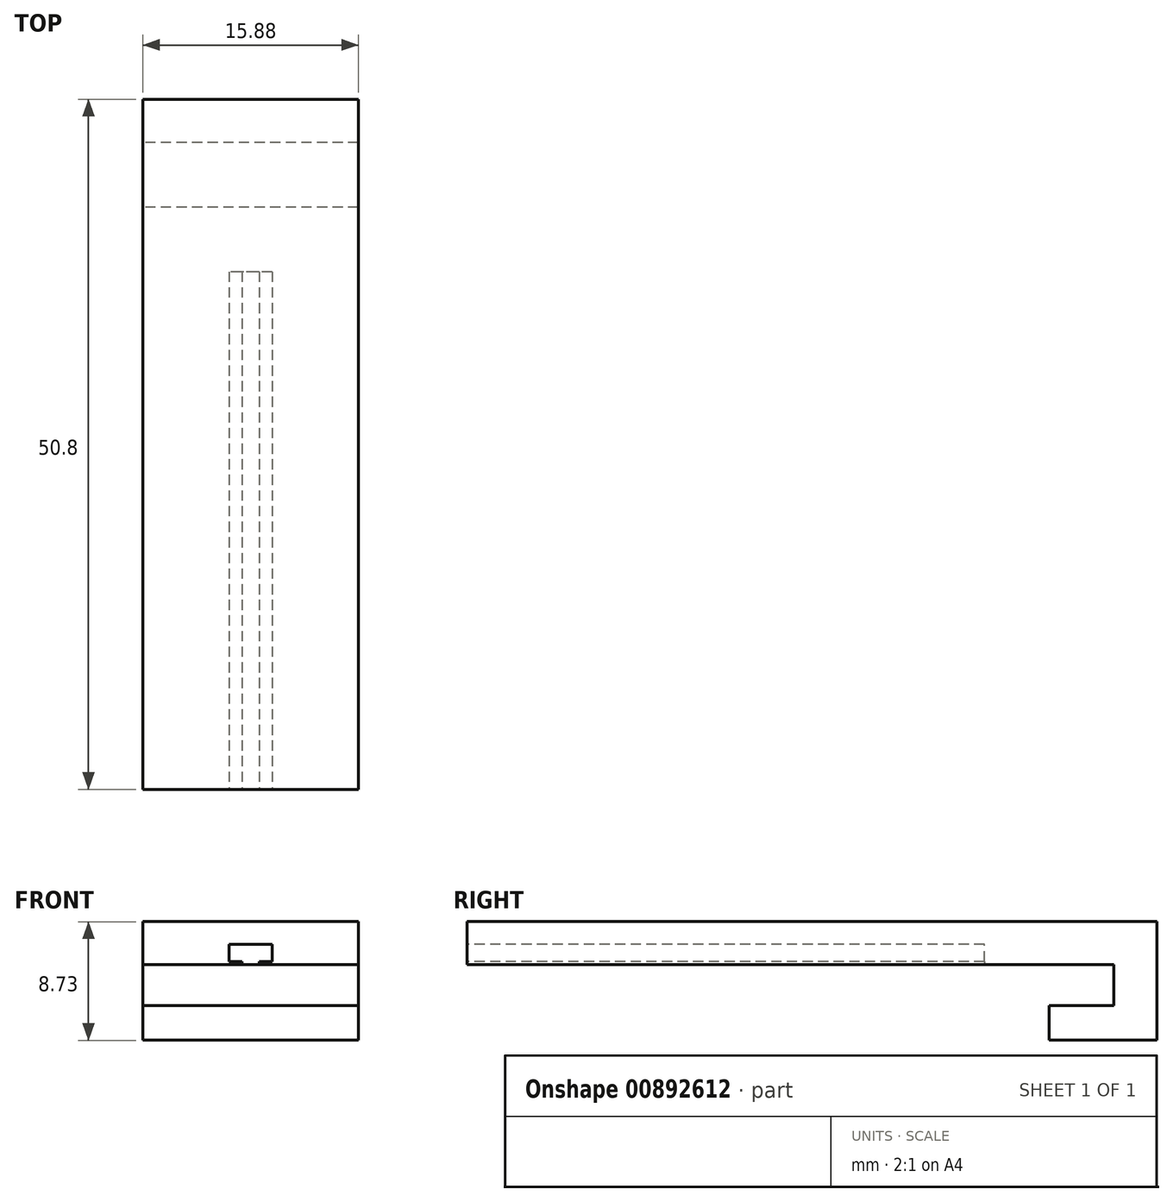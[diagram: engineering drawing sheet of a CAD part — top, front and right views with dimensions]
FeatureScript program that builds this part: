
annotation { "Feature Type Name" : "Feature", "Feature Type Description" : "" }
export const myFeature = defineFeature(function(context is Context, id is Id, definition is map)
    precondition{}
    {
        {
            var Q0;
            Q0=qCreatedBy(makeId("Top.planeOp"),FACE);
            var sketch = newSketch(context, id + "F0", { "sketchPlane" : qUnion([Q0])});
            skLineSegment(sketch, "E0.bottom", {"start": v(7.94, -25.4) * mm, "end": v(-7.94, -25.4) * mm});
            skLineSegment(sketch, "E0.top", {"start": v(7.94, 25.4) * mm, "end": v(-7.94, 25.4) * mm});
            skLineSegment(sketch, "E0.left", {"start": v(7.94, -25.4) * mm, "end": v(7.94, 25.4) * mm});
            skLineSegment(sketch, "E0.right", {"start": v(-7.94, -25.4) * mm, "end": v(-7.94, 25.4) * mm});
            skPoint(sketch, "E0.middle", {"position": v(0, 0) * mm});
            skSolve(sketch);
        }
        {
            var Q0;
            Q0=makeQuery(id+"F0.imprint","IMPRINT",FACE,{"disambiguationData":[TD([[makeQuery(id+"F0.imprint","IMPRINT",EDGE,{"derivedFrom":sQuery(id+"F0.wireOp",EDGE,"E0.bottom")}),-1.0]])]});
            extrude(context, id + "F1", {"entities" : qUnion([Q0]), "depth" : 3.17 * mm, "offsetDistance" : 25.4 * mm});
        }
        {
            var Q0;
            Q0=makeQuery(id+"F1.opExtrude","CAP_FACE",FACE,{"disambiguationData":[OSD([sQuery(id+"F0.wireOp",EDGE,"E0.bottom"),sQuery(id+"F0.wireOp",EDGE,"E0.top"),sQuery(id+"F0.wireOp",EDGE,"E0.left"),sQuery(id+"F0.wireOp",EDGE,"E0.right")])],"isStart":true});
            var sketch = newSketch(context, id + "F2", { "sketchPlane" : qUnion([Q0])});
            skLineSegment(sketch, "E1.bottom", {"start": v(7.94, -25.4) * mm, "end": v(-7.94, -25.4) * mm});
            skLineSegment(sketch, "E1.top", {"start": v(7.94, -22.23) * mm, "end": v(-7.94, -22.23) * mm});
            skLineSegment(sketch, "E1.left", {"start": v(7.94, -25.4) * mm, "end": v(7.94, -22.23) * mm});
            skLineSegment(sketch, "E1.right", {"start": v(-7.94, -25.4) * mm, "end": v(-7.94, -22.23) * mm});
            skSolve(sketch);
        }
        {
            var Q0;
            Q0=makeQuery(id+"F2.imprint","IMPRINT",FACE,{"disambiguationData":[TD([[makeQuery(id+"F2.imprint","IMPRINT",EDGE,{"derivedFrom":sQuery(id+"F2.wireOp",EDGE,"E1.bottom")}),-1.0]])]});
            extrude(context, id + "F3", {"entities" : qUnion([Q0]), "operationType" : NewBodyOperationType.ADD, "depth" : 5.56 * mm, "offsetDistance" : 25.4 * mm});
        }
        {
            var Q0;
            Q0=makeQuery(id+"F3.opExtrude","SWEPT_FACE",FACE,{"disambiguationData":[OSD([sQuery(id+"F2.wireOp",EDGE,"E1.top")])]});
            var sketch = newSketch(context, id + "F4", { "sketchPlane" : qUnion([Q0])});
            skLineSegment(sketch, "E2.bottom", {"start": v(7.94, -5.56) * mm, "end": v(-7.94, -5.56) * mm});
            skLineSegment(sketch, "E2.top", {"start": v(7.94, -3.02) * mm, "end": v(-7.94, -3.02) * mm});
            skLineSegment(sketch, "E2.left", {"start": v(7.94, -5.56) * mm, "end": v(7.94, -3.02) * mm});
            skLineSegment(sketch, "E2.right", {"start": v(-7.94, -5.56) * mm, "end": v(-7.94, -3.02) * mm});
            skSolve(sketch);
        }
        {
            var Q0;
            Q0=makeQuery(id+"F4.imprint","IMPRINT",FACE,{"disambiguationData":[TD([[makeQuery(id+"F4.imprint","IMPRINT",EDGE,{"derivedFrom":sQuery(id+"F4.wireOp",EDGE,"E2.bottom")}),-1.0]])]});
            extrude(context, id + "F5", {"entities" : qUnion([Q0]), "operationType" : NewBodyOperationType.ADD, "depth" : 4.76 * mm, "offsetDistance" : 25.4 * mm});
        }
        {
            var Q0;
            Q0=makeQuery(id+"F1.opExtrude","SWEPT_FACE",FACE,{"disambiguationData":[OSD([sQuery(id+"F0.wireOp",EDGE,"E0.bottom")])]});
            var sketch = newSketch(context, id + "F6", { "sketchPlane" : qUnion([Q0])});
            skLineSegment(sketch, "E3.bottom", {"start": v(1.59, 0.25) * mm, "end": v(-1.59, 0.25) * mm});
            skLineSegment(sketch, "E3.top", {"start": v(1.59, 1.52) * mm, "end": v(-1.59, 1.52) * mm});
            skLineSegment(sketch, "E3.left", {"start": v(1.59, 0.25) * mm, "end": v(1.59, 1.52) * mm});
            skLineSegment(sketch, "E3.right", {"start": v(-1.59, 0.25) * mm, "end": v(-1.59, 1.52) * mm});
            skPoint(sketch, "E3.middle", {"position": v(0, 0.89) * mm});
            skLineSegment(sketch, "E4.bottom", {"start": v(-0.63, 0.25) * mm, "end": v(0.64, 0.25) * mm});
            skLineSegment(sketch, "E4.top", {"start": v(-0.63, 0) * mm, "end": v(0.64, 0) * mm});
            skLineSegment(sketch, "E4.left", {"start": v(-0.63, 0.25) * mm, "end": v(-0.63, 0) * mm});
            skLineSegment(sketch, "E4.right", {"start": v(0.64, 0.25) * mm, "end": v(0.64, 0) * mm});
            skPoint(sketch, "E4.middle", {"position": v(0, 0.12) * mm});
            skPoint(sketch, "E4.middle.positionSnap0", {"position": v(0, 0.25) * mm});
            skPoint(sketch, "E4.centerSnap0", {"position": v(0, 0.25) * mm});
            skSolve(sketch);
        }
        {
            var Q0;
            Q0=makeQuery(id+"F6.imprint","IMPRINT",FACE,{"disambiguationData":[TD([[makeQuery(id+"F6.imprint","IMPRINT",EDGE,{"derivedFrom":sQuery(id+"F6.wireOp",EDGE,"E3.top")}),1.0]])]});
            var Q1;
            {var subQ0=sQuery(id+"F6.wireOp",EDGE,"E4.right");var subQ1=sQuery(id+"F6.wireOp",EDGE,"E3.bottom");var subQ2=makeQuery(id+"F6.imprint","INTERSECT",VERTEX,{"derivedFrom":[subQ1,subQ0]});Q1=makeQuery(id+"F6.imprint","IMPRINT",FACE,{"disambiguationData":[TD([[makeQuery(id+"F6.imprint","IMPRINT",EDGE,{"disambiguationData":[TD([[subQ2,-1.0]])],"derivedFrom":subQ1}),1.0]])]});}
            extrude(context, id + "F7", {"entities" : qUnion([Q0, Q1]), "operationType" : NewBodyOperationType.REMOVE, "oppositeDirection" : true, "depth" : 38.1 * mm, "offsetDistance" : 25.4 * mm});
        }
    });
